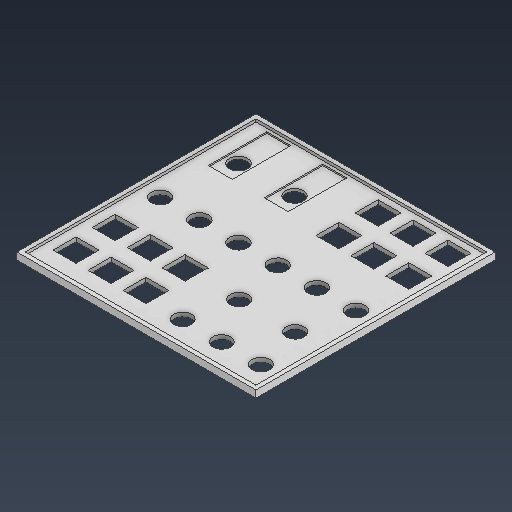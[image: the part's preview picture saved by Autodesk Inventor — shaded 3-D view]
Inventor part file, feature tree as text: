
AUTODESK INVENTOR PART (.ipt)
format: ipt  version: 2025.3 (Build 293356000, 356)  size: 293,888 bytes
history: native  units: mm
features: sketch x6, extrude x4, projected_geometry x2
ambient origin geometry x8: Origin, YZ Plane, XZ Plane, XY Plane, X Axis, Y Axis, Z Axis, Center Point
bodies: Solid1 (feature_tree)
feature tree (12):
  extrude  "Extrusion1"  Depth=171.0mm
  extrude  "Extrusion2"  Depth=2.0mm TaperAngle=0.0deg
  extrude  "Extrusion3"  Depth=1.0mm
  extrude  "Extrusion5"  Depth=60.0mm
  sketch  "Sketch1"  dims[d0=171.0mm d1=171.0mm]
  sketch  "Sketch2"  dims[d7=1.0mm d8=1.0mm]
  projected_geometry  "Projected Loop1"
  sketch  "Sketch3"  dims[d9=60.0mm d10=78.0mm]
  projected_geometry  "Projected Loop2"
  sketch  "Sketch Rectangular Pattern1"  dims[d2=3.0mm d3=0.0mm d5=2.0mm d6=0.0mm]
  sketch  "Sketch Rectangular Pattern4"  dims[d11=78.0mm]
  sketch  "Sketch5"  dims[d12=60.0mm d13=1.0mm d14=1.0mm d15=1.0mm d16=1.0mm d17=75.0mm d19=1.0mm d20=5.0mm d21=30.0mm d22=5.0mm d23=5.0mm d24=1.0mm d27=5.0mm d28=5.0mm d29=1.0mm d30=4.0mm d31=25.0mm d32=16.4mm d33=16.4mm d35=20.0mm d37=28.0mm d38=30.0mm d40=25.0mm d44=5.8mm d45=3.5mm d46=14.0mm d47=11.7mm d49=20.0mm d51=30.0mm d52=16.4mm d53=16.4mm d54=28.0mm d55=25.0mm d57=30.0mm d58=80.0mm d59=25.0mm d60=25.0mm d61=20.0mm d62=40.0mm d63=12.8mm d64=12.8mm d65=10.0mm d66=0.0mm d67=80.0mm d68=16.2mm d69=16.2mm d70=16.2mm d71=28.0mm d72=28.0mm d73=12.0mm d74=12.8mm d75=12.8mm d76=12.8mm d77=13.0mm d78=60.0mm d80=28.0mm d81=10.0mm d83=10.0mm d85=11.5mm d86=163.0mm d87=65.0mm d88=95.0mm d89=88.0mm d90=13.0mm d91=13.0mm d92=30.0mm d93=40.0mm d94=17.5mm d98=165.0mm d99=13.0mm d100=28.8mm d101=17.2mm d102=17.2mm d103=1.0mm d104=0.0mm d105=20.3mm d106=20.3mm]
